# Revit family: Specialty_Equipment-Planter-Planters_Unlimited-Modern-Akio-rev
name_source: partatom
category: Specialty Equipment
units: mm (PartAtom-declared; Revit-internal decimal feet)

## family parameters
Always vertical = Yes
Cut with Voids When Loaded = No
Enable Cutting in Views = No
Maintain Annotation Orientation = No
OmniClass Number = 23.40.05.21.17
OmniClass Title = Planters
Part Type = Normal
Room Calculation Point = No
Round Connector Dimension = Use Diameter
Shared = No
Work Plane-Based = No

## types (5) — shared parameters
Assembly Code = G2050600
Base thickness = 0' - 0 1/2"
CD_Diameter = 0' - 0"
CD_Finish = Matte-Semi Glos-Gloss-Sand
CD_Microsite = https://www.caddetails.com
CD_Offset = 0' - 0"
CD_Product Page URL = https://www.plantersunlimited.com
CD_Specification = https://www.plantersunlimited.com
Default Elevation = 0' - 0"
Description = Modular Planting Bed
Manufacturer = Planters Unlimited
Model = Lunetta Fiberglass Low Bowl Planter
Type Comments = Akio Fiberglass Low Bowl Planter
URL = https://www.plantersunlimited.com

## per-type parameters (varying)
| type | CD_Diameter Min | CD_Height | CD_Width | Width Drainage |
| 26" Dia x8"H | 0' - 8 1/2" | 0' - 8" | 2' - 2" | 0' - 1" |
| 31.5" Dia x10.5"H | 0' - 10 1/2" | 0' - 10 1/2" | 2' - 7 1/2" | 0' - 2" |
| 18" Dia x6"H | 0' - 6" | 0' - 6" | 1' - 6" | 0' - 1" |
| 43.5" Dia x17.5"H | 1' - 2 1/2" | 1' - 5 1/2" | 3' - 7 1/2" | 0' - 3" |
| 60" Dia x20"H | 1' - 8" | 1' - 8" | 5' - 0" | 0' - 3" |

## geometry (parser evidence)
native form markers: Sweep x3
no freeform markers — native parametric forms only
